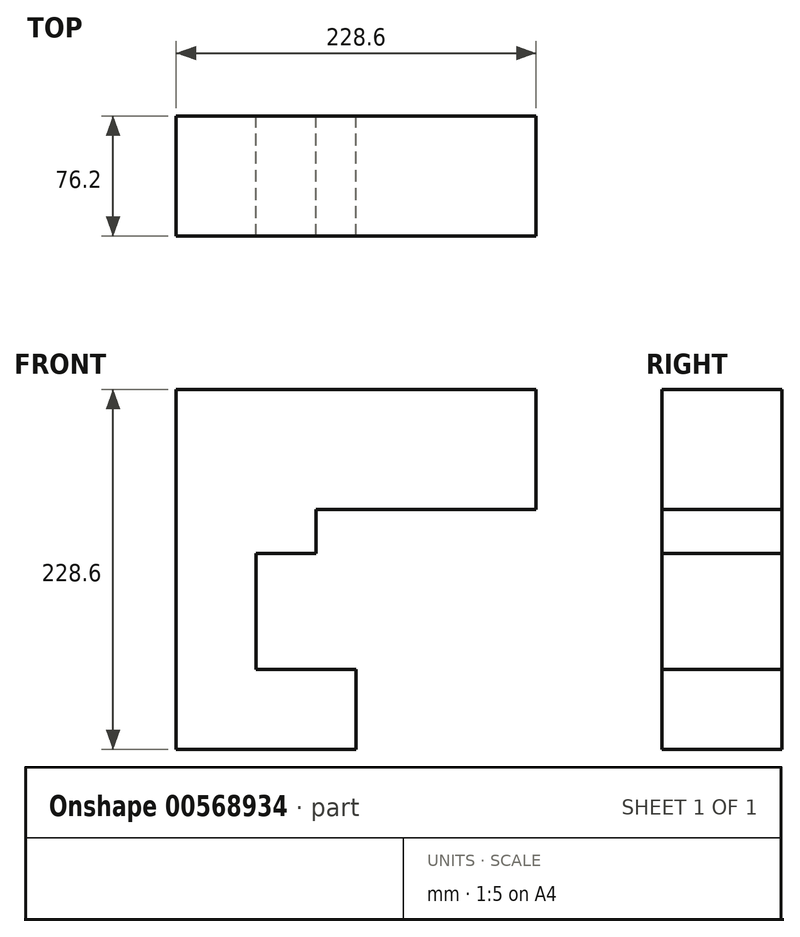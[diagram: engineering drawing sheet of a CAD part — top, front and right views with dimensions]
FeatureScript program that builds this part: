
annotation { "Feature Type Name" : "Feature", "Feature Type Description" : "" }
export const myFeature = defineFeature(function(context is Context, id is Id, definition is map)
    precondition{}
    {
        {
            var Q0;
            Q0=qCreatedBy(makeId("Front.planeOp"),FACE);
            var sketch = newSketch(context, id + "F0", { "sketchPlane" : qUnion([Q0])});
            skLineSegment(sketch, "E0.bottom", {"start": v(-141.5, 222.86) * mm, "end": v(87.1, 222.86) * mm});
            skLineSegment(sketch, "E0.left", {"start": v(-141.5, 222.86) * mm, "end": v(-141.5, -5.74) * mm});
            skLineSegment(sketch, "E1.bottom", {"start": v(87.1, 146.66) * mm, "end": v(-52.6, 146.66) * mm});
            skLineSegment(sketch, "E1.right", {"start": v(-52.6, 146.66) * mm, "end": v(-52.6, 118.78) * mm});
            skLineSegment(sketch, "E2", {"start": v(87.1, 222.86) * mm, "end": v(87.1, 146.66) * mm});
            skLineSegment(sketch, "E3", {"start": v(-52.6, 118.78) * mm, "end": v(-90.7, 118.78) * mm});
            skLineSegment(sketch, "E4", {"start": v(-90.7, 118.78) * mm, "end": v(-90.7, 45.1) * mm});
            skLineSegment(sketch, "E5", {"start": v(-141.5, -5.74) * mm, "end": v(-27.2, -5.74) * mm});
            skLineSegment(sketch, "E6", {"start": v(-90.7, 45.1) * mm, "end": v(-27.2, 45.1) * mm});
            skLineSegment(sketch, "E7", {"start": v(-27.2, 45.1) * mm, "end": v(-27.2, -5.74) * mm});
            skSolve(sketch);
        }
        {
            var Q0;
            Q0 = qSketchRegion(id + "F0", true);
            extrude(context, id + "F1", {"entities" : qUnion([Q0]), "depth" : 76.2 * mm, "offsetDistance" : 25.4 * mm});
        }
    });
